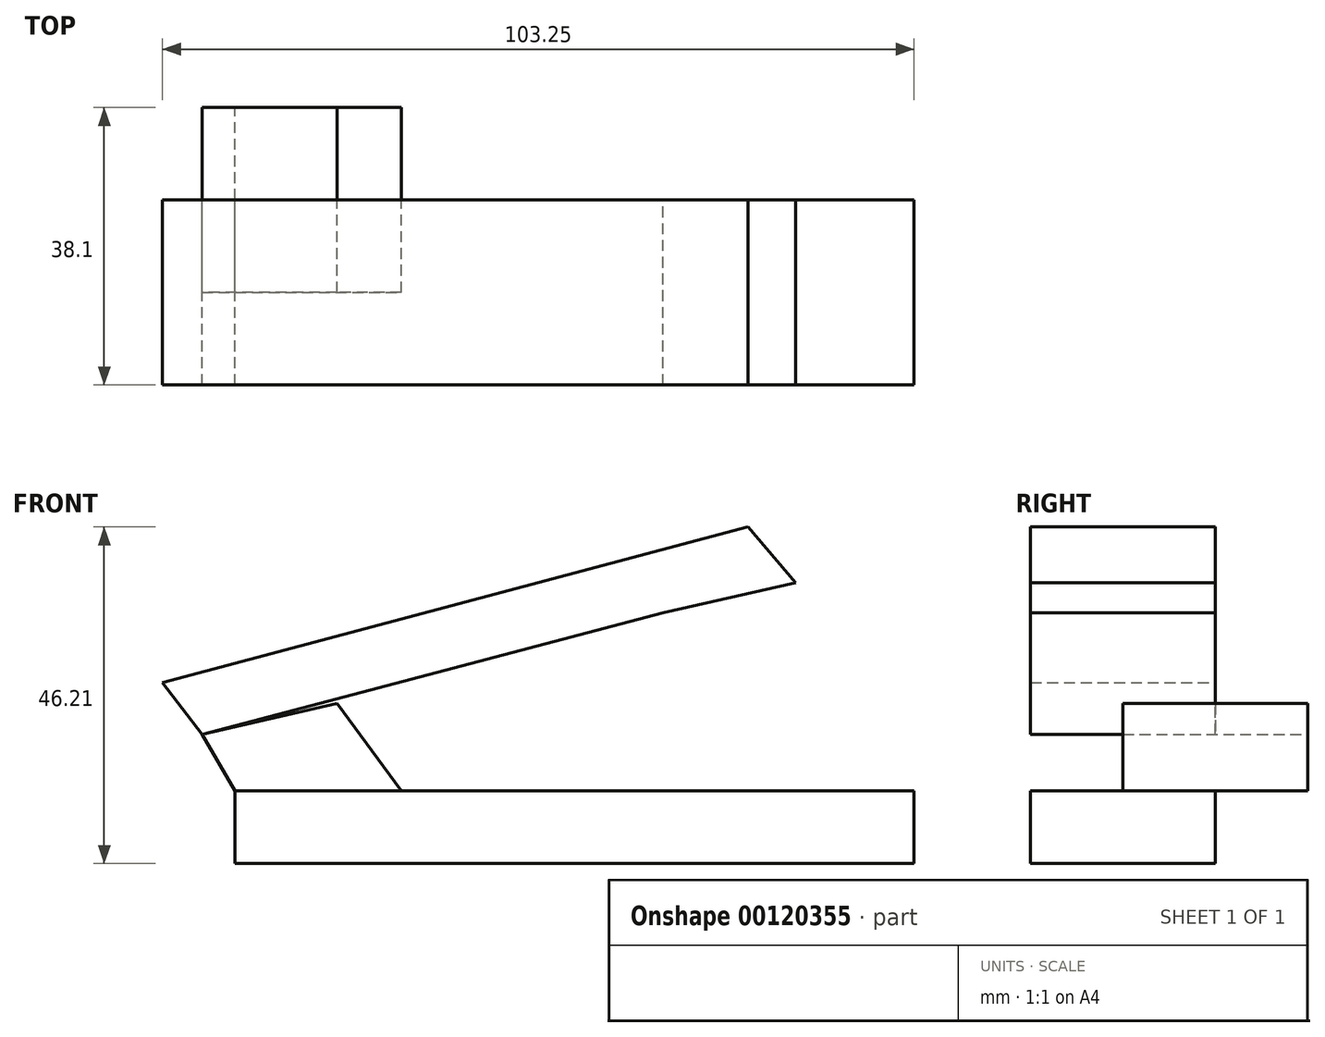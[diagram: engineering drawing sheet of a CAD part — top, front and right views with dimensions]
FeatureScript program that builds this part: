
annotation { "Feature Type Name" : "Feature", "Feature Type Description" : "" }
export const myFeature = defineFeature(function(context is Context, id is Id, definition is map)
    precondition{}
    {
        {
            var Q0;
            Q0=qCreatedBy(makeId("Front.planeOp"),FACE);
            var sketch = newSketch(context, id + "F0", { "sketchPlane" : qUnion([Q0])});
            skLineSegment(sketch, "E0.bottom", {"start": v(-46.78, 4.7) * mm, "end": v(46.5, 4.7) * mm});
            skLineSegment(sketch, "E0.top", {"start": v(-46.78, -5.28) * mm, "end": v(46.5, -5.28) * mm});
            skLineSegment(sketch, "E0.left", {"start": v(-46.78, 4.7) * mm, "end": v(-46.78, -5.28) * mm});
            skLineSegment(sketch, "E0.right", {"start": v(46.5, 4.7) * mm, "end": v(46.5, -5.28) * mm});
            skLineSegment(sketch, "E1", {"start": v(-23.96, 4.7) * mm, "end": v(-32.8, 16.69) * mm});
            skLineSegment(sketch, "E2", {"start": v(-32.8, 16.69) * mm, "end": v(-51.34, 12.4) * mm});
            skLineSegment(sketch, "E3", {"start": v(-51.34, 12.4) * mm, "end": v(-46.78, 4.7) * mm});
            skLineSegment(sketch, "E4", {"start": v(-28.38, 10.7) * mm, "end": v(13.98, 21.25) * mm});
            skLineSegment(sketch, "E5", {"start": v(13.98, 21.25) * mm, "end": v(12.02, 29.1) * mm});
            skLineSegment(sketch, "E6", {"start": v(12.02, 29.1) * mm, "end": v(-51.34, 12.4) * mm});
            skLineSegment(sketch, "E7", {"start": v(-51.34, 12.4) * mm, "end": v(-56.76, 19.54) * mm});
            skLineSegment(sketch, "E8", {"start": v(-56.76, 19.54) * mm, "end": v(23.67, 40.93) * mm});
            skLineSegment(sketch, "E9", {"start": v(23.67, 40.93) * mm, "end": v(30.24, 33.23) * mm});
            skLineSegment(sketch, "E10", {"start": v(30.24, 33.23) * mm, "end": v(12.02, 29.1) * mm});
            skSolve(sketch);
        }
        {
            var Q0;
            Q0=makeQuery(id+"F0.imprint","IMPRINT",FACE,{"disambiguationData":[TD([[makeQuery(id+"F0.imprint","IMPRINT",EDGE,{"derivedFrom":sQuery(id+"F0.wireOp",EDGE,"E6")}),-1.0]])]});
            var Q1;
            Q1=makeQuery(id+"F0.imprint","IMPRINT",FACE,{"disambiguationData":[TD([[makeQuery(id+"F0.imprint","IMPRINT",EDGE,{"derivedFrom":sQuery(id+"F0.wireOp",EDGE,"E0.top")}),1.0]])]});
            extrude(context, id + "F1", {"entities" : qUnion([Q0, Q1]), "depth" : 25.4 * mm});
        }
        {
            var Q0;
            {var subQ0=sQuery(id+"F0.wireOp",EDGE,"E2");Q0=makeQuery(id+"F0.imprint","IMPRINT",FACE,{"disambiguationData":[TD([[makeQuery(id+"F0.imprint","IMPRINT",EDGE,{"derivedFrom":subQ0}),1.0]])]});}
            extrude(context, id + "F2", {"entities" : qUnion([Q0]), "operationType" : NewBodyOperationType.ADD, "endBound" : BoundingType.SYMMETRIC, "depth" : 25.4 * mm});
        }
    });
